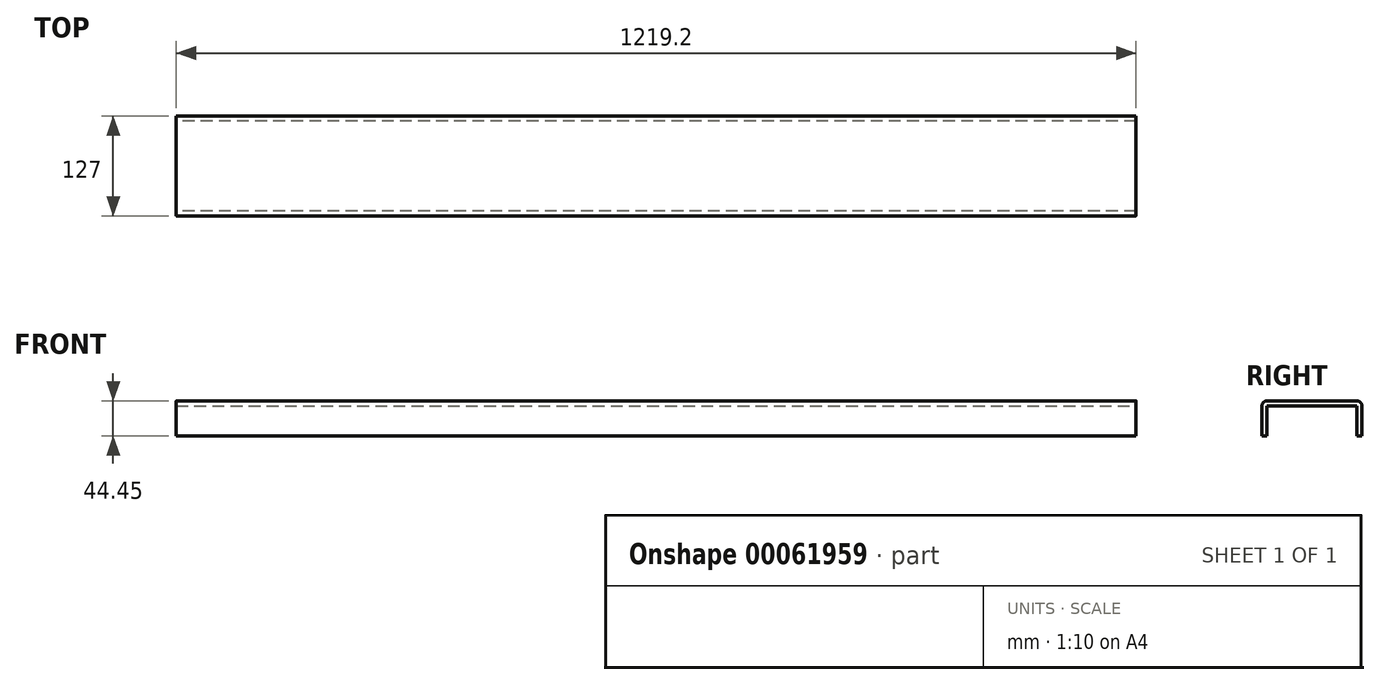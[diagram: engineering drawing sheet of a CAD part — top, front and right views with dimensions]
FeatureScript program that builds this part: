
annotation { "Feature Type Name" : "Feature", "Feature Type Description" : "" }
export const myFeature = defineFeature(function(context is Context, id is Id, definition is map)
    precondition{}
    {
        {
            var Q0;
            Q0=qCreatedBy(makeId("Right.planeOp"),FACE);
            var sketch = newSketch(context, id + "F0", { "sketchPlane" : qUnion([Q0])});
            skLineSegment(sketch, "E0", {"start": v(-63.5, 0) * mm, "end": v(63.5, 0) * mm});
            skLineSegment(sketch, "E1", {"start": v(-63.5, 0) * mm, "end": v(-63.5, -44.45) * mm});
            skLineSegment(sketch, "E2", {"start": v(-63.5, -44.45) * mm, "end": v(63.5, -44.45) * mm});
            skLineSegment(sketch, "E3", {"start": v(63.5, -44.45) * mm, "end": v(63.5, 0) * mm});
            skSolve(sketch);
        }
        {
            var Q0;
            Q0 = qSketchRegion(id + "F0", true);
            extrude(context, id + "F1", {"entities" : qUnion([Q0]), "endBound" : BoundingType.SYMMETRIC, "depth" : 1219.2 * mm});
        }
        {
            var Q0;
            Q0=makeQuery(id+"F1.opExtrude","SWEPT_EDGE",EDGE,{"disambiguationData":[OSD([sQuery(id+"F0.wireOp",EDGE,"E0"),sQuery(id+"F0.wireOp",EDGE,"E1")])]});
            var Q1;
            Q1=makeQuery(id+"F1.opExtrude","SWEPT_EDGE",EDGE,{"disambiguationData":[OSD([sQuery(id+"F0.wireOp",EDGE,"E0"),sQuery(id+"F0.wireOp",EDGE,"E3")])]});
            fillet(context, id + "F2", {"entities" : qUnion([Q0, Q1]), "radius" : 6.35 * mm, "tangentPropagation" : true, "allowEdgeOverflow" : false});
        }
        {
            var Q0;
            Q0=makeQuery(id+"F1.opExtrude","SWEPT_FACE",FACE,{"disambiguationData":[OSD([sQuery(id+"F0.wireOp",EDGE,"E2")])]});
            var Q1;
            Q1=makeQuery(id+"F1.opExtrude","CAP_FACE",FACE,{"disambiguationData":[OSD([sQuery(id+"F0.wireOp",EDGE,"E0"),sQuery(id+"F0.wireOp",EDGE,"E1"),sQuery(id+"F0.wireOp",EDGE,"E2"),sQuery(id+"F0.wireOp",EDGE,"E3")])],"isStart":false});
            var Q2;
            Q2=makeQuery(id+"F1.opExtrude","CAP_FACE",FACE,{"disambiguationData":[OSD([sQuery(id+"F0.wireOp",EDGE,"E0"),sQuery(id+"F0.wireOp",EDGE,"E1"),sQuery(id+"F0.wireOp",EDGE,"E2"),sQuery(id+"F0.wireOp",EDGE,"E3")])],"isStart":true});
            shell(context, id + "F3", {"entities" : qUnion([Q0, Q1, Q2]), "thickness" : 6.35 * mm});
        }
    });
